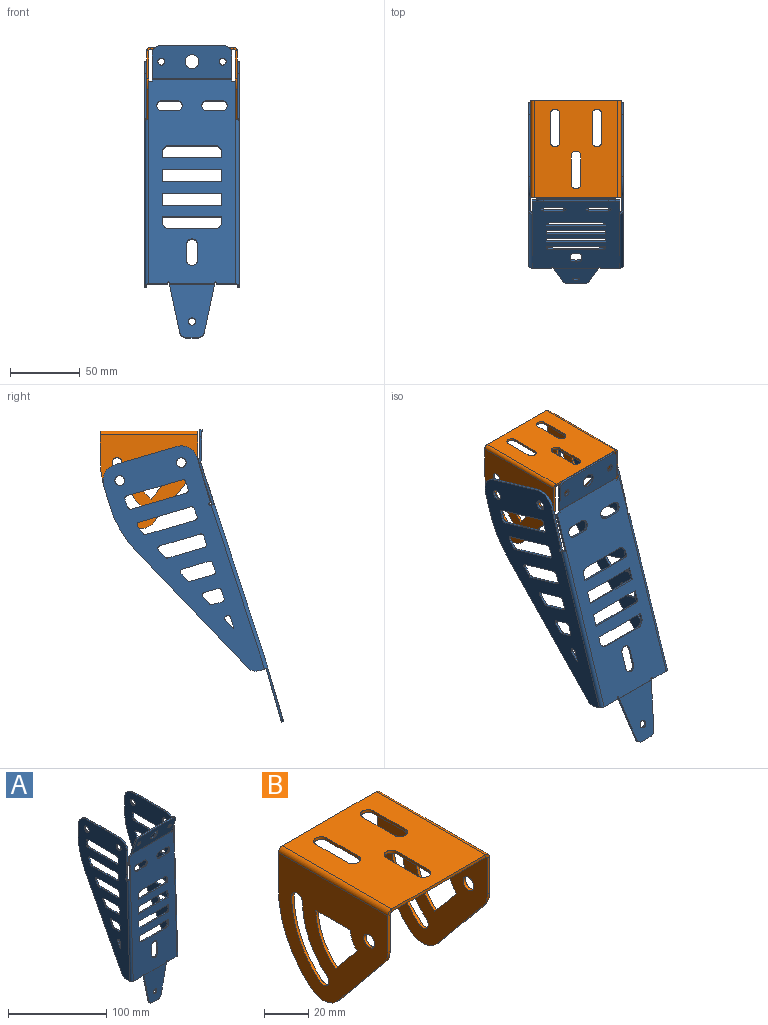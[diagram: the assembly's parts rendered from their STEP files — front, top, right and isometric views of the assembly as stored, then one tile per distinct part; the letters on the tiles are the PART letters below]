
ASSEMBLY  parts=2 mates=1
PART A: 208 faces, bbox 68x78.9x217.8 mm
  f0: plane 7.85x1.5mm, normal (0,0,-1), area 11.8mm2, adj f4,f5,f6,f7
  f1: plane 35.99x7.42mm, normal (0.98,0,-0.2), area 55.1mm2, adj f4,f5,f6,f196
  f2: cylinder r=2.75mm len=5.5mm, axis (0,-1,0), area 25.9mm2, adj f4,f5
  f3: plane 35.99x7.42mm, normal (-0.98,0,-0.2), area 55.1mm2, adj f4,f5,f7,f197
  f4: plane 39.98x32.49mm, normal (0,-1,0), area 939.2mm2, adj f0,f1,f2,f3,f6,f7,f198
  f5: plane 39.98x32.49mm, normal (0,1,0), area 939.2mm2, adj f0,f1,f2,f3,f6,f7,f199
  f6: cylinder r=5mm len=4.9mm, axis (0,-1,0), area 10.3mm2, adj f0,f1,f4,f5
  f7: cylinder r=5mm len=4.9mm, axis (0,1,0), area 10.3mm2, adj f0,f3,f4,f5
  f8: plane 33.42x1.5mm, normal (0,-1,0), area 50.1mm2, adj f9,f42,f43,f70
  f9: plane 171x74mm, normal (-1,0,0), area 6427.2mm2, adj f8,f10,f11,f12,f13,f14,f15,f16
  f10: plane 4.3x1.5mm, normal (0,0,-1), area 6.4mm2, adj f9,f43,f60,f205
  f11: plane 103.36x53.61mm, normal (0,0.89,-0.46), area 174.7mm2, adj f9,f43,f59,f60
  f12: plane 14.49x1.5mm, normal (0,1,0), area 21.7mm2, adj f9,f13,f43,f59
  f13: cylinder r=12mm len=12mm, axis (1,0,0), area 28.3mm2, adj f9,f12,f14,f43
  f14: plane 45.94x1.5mm, normal (0,0,1), area 68.9mm2, adj f9,f13,f42,f43
  f15: plane 41.22x1.5mm, normal (0,0,1), area 61.8mm2, adj f9,f43,f56,f57
  f16: plane 5.99x1.5mm, normal (0,1,-0.03), area 9mm2, adj f9,f43,f47,f56
  f17: plane 41.25x1.5mm, normal (0,0,-1), area 61.9mm2, adj f9,f43,f44,f47
  f18: plane 1.5x0.49mm, normal (0,-1,0), area 0.7mm2, adj f9,f41,f43,f44
  f19: plane 36.77x1.5mm, normal (0,0,1), area 55.2mm2, adj f9,f43,f45,f50
  f20: plane 5.99x1.5mm, normal (0,1,-0.03), area 9mm2, adj f9,f43,f48,f50
  f21: plane 38.8x1.5mm, normal (0,0,-1), area 58.2mm2, adj f9,f43,f48,f55
  f22: plane 5.99x1.5mm, normal (0,1,-0.03), area 9mm2, adj f9,f43,f51,f53
  f23: plane 30.15x1.5mm, normal (0,0,-1), area 45.2mm2, adj f9,f43,f46,f51
  f24: plane 5.97x3.1mm, normal (0,-0.89,0.46), area 10.1mm2, adj f9,f43,f46,f49
  f25: plane 5.99x1.5mm, normal (0,1,-0.03), area 9mm2, adj f9,f43,f62,f64
  f26: plane 20.16x1.5mm, normal (0,0,-1), area 30.2mm2, adj f9,f43,f58,f62
  f27: plane 5.97x3.1mm, normal (0,-0.89,0.46), area 10.1mm2, adj f9,f43,f52,f58
  f28: plane 5.99x1.5mm, normal (0,1,-0.03), area 9mm2, adj f9,f43,f66,f67
  f29: plane 10.17x1.5mm, normal (0,0,-1), area 15.3mm2, adj f9,f43,f54,f67
  f30: plane 5.98x3.1mm, normal (0,-0.89,0.46), area 10.1mm2, adj f9,f43,f54,f63
  f31: plane 8.05x1.5mm, normal (0,1,-0.03), area 12.1mm2, adj f9,f36,f43,f65
  f32: plane 1.5x0.19mm, normal (0,0,-1), area 0.3mm2, adj f9,f43,f61,f65
  f33: plane 7.07x3.67mm, normal (0,-0.89,0.46), area 11.9mm2, adj f9,f36,f43,f61
  f34: cylinder r=3.5mm len=7mm, axis (1,0,0), area 33mm2, adj f9,f43
  f35: cylinder r=3.5mm len=7mm, axis (1,0,0), area 33mm2, adj f9,f43
  f36: plane 1.5x0.55mm, normal (0,0,1), area 0.8mm2, adj f9,f31,f33,f43
  f37: plane 7.26x1.5mm, normal (0,0,1), area 10.9mm2, adj f9,f43,f63,f66
  f38: plane 17.26x1.5mm, normal (0,0,1), area 25.9mm2, adj f9,f43,f52,f64
  f39: plane 27.25x1.5mm, normal (0,0,1), area 40.9mm2, adj f9,f43,f49,f53
  f40: cylinder r=68.1mm len=6.14mm, axis (1,0,0), area 9.8mm2, adj f9,f43,f45,f55
  f41: cylinder r=68.1mm len=5.64mm, axis (1,0,0), area 8.5mm2, adj f9,f18,f43,f57
  f42: cylinder r=12mm len=12.06mm, axis (1,0,0), area 28.4mm2, adj f8,f9,f14,f43
  f43: plane 171x74mm, normal (1,0,0), area 6427.2mm2, adj f8,f10,f11,f12,f13,f14,f15,f16
  f44: cylinder r=2mm len=2mm, axis (-1,0,0), area 4.7mm2, adj f9,f17,f18,f43
  f45: cylinder r=2mm len=1.84mm, axis (1,0,0), area 3.5mm2, adj f9,f19,f40,f43
  f46: cylinder r=2mm len=2.92mm, axis (-1,0,0), area 6.1mm2, adj f9,f23,f24,f43
  f47: cylinder r=2mm len=2mm, axis (-1,0,0), area 4.6mm2, adj f9,f16,f17,f43
  f48: cylinder r=2mm len=2mm, axis (-1,0,0), area 4.6mm2, adj f9,f20,f21,f43
  f49: cylinder r=2mm len=1.78mm, axis (-1,0,0), area 3.3mm2, adj f9,f24,f39,f43
  f50: cylinder r=2mm len=2.06mm, axis (-1,0,0), area 4.8mm2, adj f9,f19,f20,f43
  f51: cylinder r=2mm len=2mm, axis (-1,0,0), area 4.6mm2, adj f9,f22,f23,f43
  f52: cylinder r=2mm len=1.78mm, axis (-1,0,0), area 3.3mm2, adj f9,f27,f38,f43
  f53: cylinder r=2mm len=2.06mm, axis (-1,0,0), area 4.8mm2, adj f9,f22,f39,f43
  f54: cylinder r=2mm len=2.92mm, axis (-1,0,0), area 6.1mm2, adj f9,f29,f30,f43
  f55: cylinder r=2mm len=2.61mm, axis (1,0,0), area 5.6mm2, adj f9,f21,f40,f43
  f56: cylinder r=2mm len=2.06mm, axis (-1,0,0), area 4.8mm2, adj f9,f15,f16,f43
  f57: cylinder r=2mm len=1.99mm, axis (1,0,0), area 4.5mm2, adj f9,f15,f41,f43
  f58: cylinder r=2mm len=2.92mm, axis (-1,0,0), area 6.1mm2, adj f9,f26,f27,f43
  f59: cylinder r=80mm len=36.84mm, axis (1,0,0), area 57.4mm2, adj f9,f11,f12,f43
  f60: cylinder r=8mm len=7.1mm, axis (-1,0,0), area 13.1mm2, adj f9,f10,f11,f43
  f61: cylinder r=2mm len=2.92mm, axis (-1,0,0), area 6.1mm2, adj f9,f32,f33,f43
  f62: cylinder r=2mm len=2mm, axis (-1,0,0), area 4.6mm2, adj f9,f25,f26,f43
  f63: cylinder r=2mm len=1.78mm, axis (-1,0,0), area 3.3mm2, adj f9,f30,f37,f43
  f64: cylinder r=2mm len=2.06mm, axis (-1,0,0), area 4.8mm2, adj f9,f25,f38,f43
  f65: cylinder r=2mm len=2mm, axis (-1,0,0), area 4.6mm2, adj f9,f31,f32,f43
  f66: cylinder r=2mm len=2.06mm, axis (-1,0,0), area 4.8mm2, adj f9,f28,f37,f43
  f67: cylinder r=2mm len=2mm, axis (-1,0,0), area 4.6mm2, adj f9,f28,f29,f43
  f68: cylinder r=0.8mm len=1.59mm, axis (-1,0,0), area 3.8mm2, adj f9,f43,f69,f70
  f69: plane 1.5x0.7mm, normal (0,0.03,1), area 1.1mm2, adj f9,f43,f68,f204
  f70: plane 1.5x0.75mm, normal (0,-0.03,-1), area 1.1mm2, adj f8,f9,f43,f68
  f71: plane 1.5x0.19mm, normal (0,0,-1), area 0.3mm2, adj f105,f106,f112,f113
  f72: plane 8.05x1.5mm, normal (0,1,-0.03), area 12.1mm2, adj f73,f105,f106,f112
  f73: plane 1.5x0.55mm, normal (0,0,1), area 0.8mm2, adj f72,f102,f105,f106
  f74: plane 10.17x1.5mm, normal (0,0,-1), area 15.3mm2, adj f105,f106,f109,f111
  f75: plane 5.99x1.5mm, normal (0,1,-0.03), area 9mm2, adj f105,f106,f107,f109
  f76: plane 7.26x1.5mm, normal (0,0,1), area 10.9mm2, adj f105,f106,f107,f116
  f77: plane 20.16x1.5mm, normal (0,0,-1), area 30.2mm2, adj f105,f106,f119,f124
  f78: plane 5.99x1.5mm, normal (0,1,-0.03), area 9mm2, adj f105,f106,f108,f119
  f79: plane 17.26x1.5mm, normal (0,0,1), area 25.9mm2, adj f105,f106,f108,f121
  f80: plane 30.15x1.5mm, normal (0,0,-1), area 45.2mm2, adj f105,f106,f122,f127
  f81: plane 5.99x1.5mm, normal (0,1,-0.03), area 9mm2, adj f105,f106,f120,f122
  f82: plane 27.25x1.5mm, normal (0,0,1), area 40.9mm2, adj f105,f106,f120,f126
  f83: plane 38.8x1.5mm, normal (0,0,-1), area 58.2mm2, adj f105,f106,f118,f125
  f84: plane 5.99x1.5mm, normal (0,1,-0.03), area 9mm2, adj f105,f106,f123,f125
  f85: plane 36.77x1.5mm, normal (0,0,1), area 55.2mm2, adj f105,f106,f123,f128
  f86: plane 1.5x0.49mm, normal (0,-1,0), area 0.7mm2, adj f97,f105,f106,f130
  f87: plane 41.25x1.5mm, normal (0,0,-1), area 61.9mm2, adj f105,f106,f114,f130
  f88: plane 5.99x1.5mm, normal (0,1,-0.03), area 9mm2, adj f105,f106,f114,f115
  f89: plane 41.22x1.5mm, normal (0,0,1), area 61.8mm2, adj f105,f106,f115,f129
  f90: plane 45.94x1.5mm, normal (0,0,1), area 68.9mm2, adj f91,f96,f105,f106
  f91: cylinder r=12mm len=12mm, axis (1,0,0), area 28.3mm2, adj f90,f92,f105,f106
  f92: plane 14.49x1.5mm, normal (0,1,0), area 21.7mm2, adj f91,f105,f106,f117
  f93: plane 103.36x53.61mm, normal (0,0.89,-0.46), area 174.7mm2, adj f105,f106,f110,f117
  f94: plane 4.3x1.5mm, normal (0,0,-1), area 6.4mm2, adj f105,f106,f110,f201
  f95: plane 33.42x1.5mm, normal (0,-1,0), area 50.1mm2, adj f96,f105,f106,f131
  f96: cylinder r=12mm len=12.06mm, axis (1,0,0), area 28.4mm2, adj f90,f95,f105,f106
  f97: cylinder r=68.1mm len=5.64mm, axis (1,0,0), area 8.5mm2, adj f86,f105,f106,f129
  f98: cylinder r=68.1mm len=6.14mm, axis (1,0,0), area 9.8mm2, adj f105,f106,f118,f128
  f99: plane 5.97x3.1mm, normal (0,-0.89,0.46), area 10.1mm2, adj f105,f106,f126,f127
  f100: plane 5.97x3.1mm, normal (0,-0.89,0.46), area 10.1mm2, adj f105,f106,f121,f124
  f101: plane 5.98x3.1mm, normal (0,-0.89,0.46), area 10.1mm2, adj f105,f106,f111,f116
  f102: plane 7.07x3.67mm, normal (0,-0.89,0.46), area 11.9mm2, adj f73,f105,f106,f113
  f103: cylinder r=3.5mm len=7mm, axis (1,0,0), area 33mm2, adj f105,f106
  f104: cylinder r=3.5mm len=7mm, axis (1,0,0), area 33mm2, adj f105,f106
  f105: plane 171x74mm, normal (-1,0,0), area 6427.2mm2, adj f71,f72,f73,f74,f75,f76,f77,f78
  f106: plane 171x74mm, normal (1,0,0), area 6427.2mm2, adj f71,f72,f73,f74,f75,f76,f77,f78
  f107: cylinder r=2mm len=2.06mm, axis (1,0,0), area 4.8mm2, adj f75,f76,f105,f106
  f108: cylinder r=2mm len=2.06mm, axis (1,0,0), area 4.8mm2, adj f78,f79,f105,f106
  f109: cylinder r=2mm len=2mm, axis (1,0,0), area 4.6mm2, adj f74,f75,f105,f106
  f110: cylinder r=8mm len=7.1mm, axis (1,0,0), area 13.1mm2, adj f93,f94,f105,f106
  f111: cylinder r=2mm len=2.92mm, axis (1,0,0), area 6.1mm2, adj f74,f101,f105,f106
  f112: cylinder r=2mm len=2mm, axis (1,0,0), area 4.6mm2, adj f71,f72,f105,f106
  f113: cylinder r=2mm len=2.92mm, axis (1,0,0), area 6.1mm2, adj f71,f102,f105,f106
  f114: cylinder r=2mm len=2mm, axis (1,0,0), area 4.6mm2, adj f87,f88,f105,f106
  f115: cylinder r=2mm len=2.06mm, axis (1,0,0), area 4.8mm2, adj f88,f89,f105,f106
  f116: cylinder r=2mm len=1.78mm, axis (1,0,0), area 3.3mm2, adj f76,f101,f105,f106
  f117: cylinder r=80mm len=36.84mm, axis (-1,0,0), area 57.4mm2, adj f92,f93,f105,f106
  f118: cylinder r=2mm len=2.61mm, axis (1,0,0), area 5.6mm2, adj f83,f98,f105,f106
  f119: cylinder r=2mm len=2mm, axis (1,0,0), area 4.6mm2, adj f77,f78,f105,f106
  f120: cylinder r=2mm len=2.06mm, axis (1,0,0), area 4.8mm2, adj f81,f82,f105,f106
  f121: cylinder r=2mm len=1.78mm, axis (1,0,0), area 3.3mm2, adj f79,f100,f105,f106
  f122: cylinder r=2mm len=2mm, axis (1,0,0), area 4.6mm2, adj f80,f81,f105,f106
  f123: cylinder r=2mm len=2.06mm, axis (1,0,0), area 4.8mm2, adj f84,f85,f105,f106
  f124: cylinder r=2mm len=2.92mm, axis (1,0,0), area 6.1mm2, adj f77,f100,f105,f106
  f125: cylinder r=2mm len=2mm, axis (1,0,0), area 4.6mm2, adj f83,f84,f105,f106
  f126: cylinder r=2mm len=1.78mm, axis (1,0,0), area 3.3mm2, adj f82,f99,f105,f106
  f127: cylinder r=2mm len=2.92mm, axis (1,0,0), area 6.1mm2, adj f80,f99,f105,f106
  f128: cylinder r=2mm len=1.84mm, axis (1,0,0), area 3.5mm2, adj f85,f98,f105,f106
  f129: cylinder r=2mm len=1.99mm, axis (1,0,0), area 4.5mm2, adj f89,f97,f105,f106
  f130: cylinder r=2mm len=2mm, axis (1,0,0), area 4.7mm2, adj f86,f87,f105,f106
  f131: plane 1.5x0.75mm, normal (0,-0.03,-1), area 1.1mm2, adj f95,f105,f106,f132
  f132: cylinder r=0.8mm len=1.59mm, axis (1,0,0), area 3.8mm2, adj f105,f106,f131,f133
  f133: plane 1.5x0.7mm, normal (0,0.03,1), area 1.1mm2, adj f105,f106,f132,f200
  f134: plane 29.09x2.44mm, normal (-1,0,0), area 43.6mm2, adj f136,f137,f138,f200
  f135: plane 13.66x1.5mm, normal (0,-0.03,-1), area 20.5mm2, adj f136,f137,f179,f201
  f136: plane 154.56x63mm, normal (0,-1,0.03), area 7809.2mm2, adj f134,f135,f138,f139,f140,f141,f142,f143
  f137: plane 154.56x63mm, normal (0,1,-0.03), area 7809.2mm2, adj f134,f135,f138,f139,f140,f141,f142,f143
  f138: plane 3x1.5mm, normal (0,0.03,1), area 4.5mm2, adj f134,f136,f137,f180
  f139: plane 13.66x1.5mm, normal (0,-0.03,-1), area 20.5mm2, adj f136,f137,f174,f205
  f140: plane 29.09x2.44mm, normal (1,0,0), area 43.6mm2, adj f136,f137,f169,f204
  f141: plane 10.25x1.5mm, normal (0,-0.03,-1), area 15.4mm2, adj f136,f137,f142,f168
  f142: cylinder r=4mm len=8.04mm, axis (0,1,-0.03), area 18.8mm2, adj f136,f137,f141,f143
  f143: plane 10.25x1.5mm, normal (0,0.03,1), area 15.4mm2, adj f136,f137,f142,f168
  f144: plane 10.25x1.5mm, normal (0,-0.03,-1), area 15.4mm2, adj f136,f137,f145,f167
  f145: cylinder r=4mm len=8.04mm, axis (0,1,-0.03), area 18.8mm2, adj f136,f137,f144,f146
  f146: plane 10.25x1.5mm, normal (0,0.03,1), area 15.4mm2, adj f136,f137,f145,f167
  f147: plane 4.05x1.63mm, normal (1,0,0), area 6mm2, adj f136,f137,f166,f171
  f148: plane 32.5x1.5mm, normal (0,-0.03,-1), area 48.7mm2, adj f136,f137,f170,f171
  f149: plane 4.05x1.63mm, normal (-1,0,0), area 6mm2, adj f136,f137,f166,f170
  f150: plane 9.04x1.79mm, normal (1,0,0), area 13.5mm2, adj f136,f137,f151,f165
  f151: plane 42.5x1.5mm, normal (0,-0.03,-1), area 63.7mm2, adj f136,f137,f150,f152
  f152: plane 9.04x1.79mm, normal (-1,0,0), area 13.5mm2, adj f136,f137,f151,f165
  f153: plane 9.04x1.79mm, normal (-1,0,0), area 13.5mm2, adj f136,f137,f154,f164
  f154: plane 42.5x1.5mm, normal (0,0.03,1), area 63.8mm2, adj f136,f137,f153,f155
  f155: plane 9.04x1.79mm, normal (1,0,0), area 13.5mm2, adj f136,f137,f154,f164
  f156: plane 4.05x1.63mm, normal (1,0,0), area 6mm2, adj f136,f137,f157,f173
  f157: plane 42.5x1.5mm, normal (0,-0.03,-1), area 63.8mm2, adj f136,f137,f156,f158
  f158: plane 4.05x1.63mm, normal (-1,0,0), area 6mm2, adj f136,f137,f157,f172
  f159: plane 12.04x1.89mm, normal (1,0,0), area 18mm2, adj f136,f137,f160,f162
  f160: cylinder r=4mm len=8mm, axis (0,1,-0.03), area 18.8mm2, adj f136,f137,f159,f161
  f161: plane 12.04x1.89mm, normal (-1,0,0), area 18mm2, adj f136,f137,f160,f162
  f162: cylinder r=4mm len=8mm, axis (0,1,-0.03), area 18.8mm2, adj f136,f137,f159,f161
  f163: plane 32.5x1.5mm, normal (0,0.03,1), area 48.7mm2, adj f136,f137,f172,f173
  f164: plane 42.5x1.5mm, normal (0,-0.03,-1), area 63.7mm2, adj f136,f137,f153,f155
  f165: plane 42.5x1.5mm, normal (0,0.03,1), area 63.7mm2, adj f136,f137,f150,f152
  f166: plane 42.5x1.5mm, normal (0,0.03,1), area 63.7mm2, adj f136,f137,f147,f149
  f167: cylinder r=4mm len=8.04mm, axis (0,1,-0.03), area 18.8mm2, adj f136,f137,f144,f146
  f168: cylinder r=4mm len=8.04mm, axis (0,1,-0.03), area 18.8mm2, adj f136,f137,f141,f143
  f169: plane 3x1.5mm, normal (0,0.03,1), area 4.5mm2, adj f136,f137,f140,f181
  f170: cylinder r=5mm len=5.05mm, axis (0,1,-0.03), area 11.8mm2, adj f136,f137,f148,f149
  f171: cylinder r=5mm len=5.05mm, axis (0,1,-0.03), area 11.8mm2, adj f136,f137,f147,f148
  f172: cylinder r=5mm len=5.05mm, axis (0,1,-0.03), area 11.8mm2, adj f136,f137,f158,f163
  f173: cylinder r=5mm len=5.05mm, axis (0,1,-0.03), area 11.8mm2, adj f136,f137,f156,f163
  f174: plane 1.52x0.77mm, normal (-1,0,0), area 1.1mm2, adj f136,f137,f139,f175
  f175: cylinder r=0.8mm len=1.59mm, axis (0,1,-0.03), area 3.8mm2, adj f136,f137,f174,f176
  f176: plane 1.52x0.75mm, normal (1,0,0), area 1.1mm2, adj f136,f137,f175,f196
  f177: plane 1.52x0.75mm, normal (-1,0,0), area 1.1mm2, adj f136,f137,f178,f197
  f178: cylinder r=0.8mm len=1.59mm, axis (0,1,-0.03), area 3.8mm2, adj f136,f137,f177,f179
  f179: plane 1.52x0.77mm, normal (1,0,0), area 1.1mm2, adj f135,f136,f137,f178
  f180: plane 1.55x1.55mm, normal (-1,0,0), area 2.3mm2, adj f136,f137,f138,f192
  f181: plane 1.55x1.55mm, normal (1,0,0), area 2.3mm2, adj f136,f137,f169,f193
  f182: plane 47x1.43mm, normal (0,-0.31,0.95), area 70.5mm2, adj f188,f189,f190,f191
  f183: plane 18.1x7.21mm, normal (-1,0,0), area 27.8mm2, adj f188,f189,f190,f192
  f184: cylinder r=2.5mm len=5.22mm, axis (0,-0.95,-0.31), area 23.6mm2, adj f188,f189
  f185: cylinder r=2.5mm len=5.22mm, axis (0,-0.95,-0.31), area 23.6mm2, adj f188,f189
  f186: cylinder r=5mm len=10mm, axis (0,-0.95,-0.31), area 47.1mm2, adj f188,f189
  f187: plane 18.1x7.21mm, normal (1,0,0), area 27.8mm2, adj f188,f189,f191,f193
  f188: plane 57x22.39mm, normal (0,-0.95,-0.31), area 1214.3mm2, adj f182,f183,f184,f185,f186,f187,f190,f191
  f189: plane 57x22.39mm, normal (0,0.95,0.31), area 1214.3mm2, adj f182,f183,f184,f185,f186,f187,f190,f191
  f190: cylinder r=5mm len=5.22mm, axis (0,-0.95,-0.31), area 11.8mm2, adj f182,f183,f188,f189
  f191: cylinder r=5mm len=5.22mm, axis (0,-0.95,-0.31), area 11.8mm2, adj f182,f187,f188,f189
  f192: plane 1.55x0.86mm, normal (-1,0,0), area 0.9mm2, adj f180,f183,f194,f195
  f193: plane 1.55x0.86mm, normal (1,0,0), area 0.9mm2, adj f181,f187,f194,f195
  f194: cylinder r=2.5mm len=57mm, axis (-1,0,0), area 49.7mm2, adj f137,f189,f192,f193
  f195: cylinder r=1mm len=57mm, axis (-1,0,0), area 19.9mm2, adj f136,f188,f192,f193
  f196: plane 1.5x0.08mm, normal (1,0,0), area 0.1mm2, adj f1,f176,f198,f199
  f197: plane 1.5x0.08mm, normal (-1,0,0), area 0.1mm2, adj f3,f177,f198,f199
  f198: cylinder r=2.5mm len=32.49mm, axis (1,0,0), area 2.6mm2, adj f4,f136,f196,f197
  f199: cylinder r=1mm len=32.49mm, axis (1,0,0), area 1mm2, adj f5,f137,f196,f197
  f200: plane 2.5x2.5mm, normal (0,0.03,1), area 4.1mm2, adj f133,f134,f202,f203
  f201: bspline ~2.5x2.5mm, area 4.1mm2, adj f94,f135,f202,f203
  f202: cylinder r=2.5mm len=124.1mm, axis (0,0.03,1), area 487.2mm2, adj f105,f136,f200,f201
  f203: cylinder r=1mm len=124.05mm, axis (0,0.03,1), area 194.9mm2, adj f106,f137,f200,f201
  f204: plane 2.5x2.5mm, normal (0,0.03,1), area 4.1mm2, adj f69,f140,f206,f207
  f205: bspline ~2.5x2.5mm, area 4.1mm2, adj f10,f139,f206,f207
  f206: cylinder r=2.5mm len=124.1mm, axis (0,0.03,1), area 487.2mm2, adj f43,f136,f204,f205
  f207: cylinder r=1mm len=124.05mm, axis (0,0.03,1), area 194.9mm2, adj f9,f137,f204,f205
PART B: 58 faces, bbox 65x70x70 mm
  f0: plane 20x1.5mm, normal (-1,0,0), area 30mm2, adj f1,f13,f14,f15
  f1: cylinder r=3.5mm len=7mm, axis (0,0,1), area 16.5mm2, adj f0,f2,f14,f15
  f2: plane 20x1.5mm, normal (1,0,0), area 30mm2, adj f1,f13,f14,f15
  f3: plane 20x1.5mm, normal (-1,0,0), area 30mm2, adj f4,f12,f14,f15
  f4: cylinder r=3.5mm len=7mm, axis (0,0,1), area 16.5mm2, adj f3,f5,f14,f15
  f5: plane 20x1.5mm, normal (1,0,0), area 30mm2, adj f4,f12,f14,f15
  f6: plane 20x1.5mm, normal (1,0,0), area 30mm2, adj f7,f11,f14,f15
  f7: cylinder r=3.5mm len=7mm, axis (0,0,1), area 16.5mm2, adj f6,f8,f14,f15
  f8: plane 20x1.5mm, normal (-1,0,0), area 30mm2, adj f7,f11,f14,f15
  f9: plane 60x1.5mm, normal (0,1,0), area 90mm2, adj f14,f15,f34,f54
  f10: plane 60x1.5mm, normal (0,-1,0), area 90mm2, adj f14,f15,f33,f55
  f11: cylinder r=3.5mm len=7mm, axis (0,0,1), area 16.5mm2, adj f6,f8,f14,f15
  f12: cylinder r=3.5mm len=7mm, axis (0,0,1), area 16.5mm2, adj f3,f5,f14,f15
  f13: cylinder r=3.5mm len=7mm, axis (0,0,1), area 16.5mm2, adj f0,f2,f14,f15
  f14: plane 70x60mm, normal (0,0,1), area 3664.5mm2, adj f0,f1,f2,f3,f4,f5,f6,f7
  f15: plane 70x60mm, normal (0,0,-1), area 3664.5mm2, adj f0,f1,f2,f3,f4,f5,f6,f7
  f16: plane 20x1.5mm, normal (0,1,0), area 30mm2, adj f30,f31,f32,f34
  f17: plane 20x1.5mm, normal (0,-1,0), area 30mm2, adj f18,f31,f32,f33
  f18: cylinder r=12mm len=7.63mm, axis (1,0,0), area 12.4mm2, adj f17,f19,f31,f32
  f19: plane 35.5x29.25mm, normal (0,-0.77,-0.64), area 69mm2, adj f18,f20,f31,f32
  f20: cylinder r=12mm len=16.89mm, axis (1,0,0), area 28.3mm2, adj f19,f30,f31,f32
  f21: plane 16.98x13.99mm, normal (0,0.77,0.64), area 33mm2, adj f22,f29,f31,f32
  f22: cylinder r=12mm len=9.26mm, axis (1,0,0), area 15.9mm2, adj f21,f23,f31,f32
  f23: plane 22x1.5mm, normal (0,0,-1), area 33mm2, adj f22,f29,f31,f32
  f24: cylinder r=49.5mm len=38.2mm, axis (1,0,0), area 65.5mm2, adj f25,f27,f31,f32
  f25: cylinder r=3.5mm len=6.2mm, axis (1,0,0), area 16.5mm2, adj f24,f26,f31,f32
  f26: cylinder r=42.5mm len=32.8mm, axis (1,0,0), area 56.2mm2, adj f25,f27,f31,f32
  f27: cylinder r=3.5mm len=7mm, axis (1,0,0), area 16.5mm2, adj f24,f26,f31,f32
  f28: cylinder r=3.5mm len=7mm, axis (1,0,0), area 33mm2, adj f31,f32
  f29: cylinder r=34mm len=26.24mm, axis (1,0,0), area 45mm2, adj f21,f23,f31,f32
  f30: cylinder r=58mm len=44.76mm, axis (1,0,0), area 76.7mm2, adj f16,f20,f31,f32
  f31: plane 70x67.5mm, normal (1,0,0), area 2790.6mm2, adj f16,f17,f18,f19,f20,f21,f22,f23
  f32: plane 70x67.5mm, normal (-1,0,0), area 2790.6mm2, adj f16,f17,f18,f19,f20,f21,f22,f23
  f33: plane 2.5x2.5mm, normal (0,-1,0), area 4.1mm2, adj f10,f17,f35,f36
  f34: plane 2.5x2.5mm, normal (0,1,0), area 4.1mm2, adj f9,f16,f35,f36
  f35: cylinder r=2.5mm len=70mm, axis (0,-1,0), area 274.9mm2, adj f14,f31,f33,f34
  f36: cylinder r=1mm len=70mm, axis (0,-1,0), area 110mm2, adj f15,f32,f33,f34
  f37: cylinder r=12mm len=16.89mm, axis (-1,0,0), area 28.3mm2, adj f38,f51,f52,f53
  f38: plane 35.5x29.25mm, normal (0,-0.77,-0.64), area 69mm2, adj f37,f39,f52,f53
  f39: cylinder r=12mm len=7.63mm, axis (-1,0,0), area 12.4mm2, adj f38,f40,f52,f53
  f40: plane 20x1.5mm, normal (0,-1,0), area 30mm2, adj f39,f52,f53,f55
  f41: plane 20x1.5mm, normal (0,1,0), area 30mm2, adj f51,f52,f53,f54
  f42: cylinder r=42.5mm len=32.8mm, axis (-1,0,0), area 56.2mm2, adj f43,f50,f52,f53
  f43: cylinder r=3.5mm len=6.2mm, axis (-1,0,0), area 16.5mm2, adj f42,f44,f52,f53
  f44: cylinder r=49.5mm len=38.2mm, axis (-1,0,0), area 65.5mm2, adj f43,f50,f52,f53
  f45: plane 22x1.5mm, normal (0,0,-1), area 33mm2, adj f46,f49,f52,f53
  f46: cylinder r=12mm len=9.26mm, axis (-1,0,0), area 15.9mm2, adj f45,f47,f52,f53
  f47: plane 16.98x13.99mm, normal (0,0.77,0.64), area 33mm2, adj f46,f49,f52,f53
  f48: cylinder r=3.5mm len=7mm, axis (-1,0,0), area 33mm2, adj f52,f53
  f49: cylinder r=34mm len=26.24mm, axis (-1,0,0), area 45mm2, adj f45,f47,f52,f53
  f50: cylinder r=3.5mm len=7mm, axis (-1,0,0), area 16.5mm2, adj f42,f44,f52,f53
  f51: cylinder r=58mm len=44.76mm, axis (-1,0,0), area 76.7mm2, adj f37,f41,f52,f53
  f52: plane 70x67.5mm, normal (-1,0,0), area 2790.6mm2, adj f37,f38,f39,f40,f41,f42,f43,f44
  f53: plane 70x67.5mm, normal (1,0,0), area 2790.6mm2, adj f37,f38,f39,f40,f41,f42,f43,f44
  f54: plane 2.5x2.5mm, normal (0,1,0), area 4.1mm2, adj f9,f41,f56,f57
  f55: plane 2.5x2.5mm, normal (0,-1,0), area 4.1mm2, adj f10,f40,f56,f57
  f56: cylinder r=2.5mm len=70mm, axis (0,1,0), area 274.9mm2, adj f14,f52,f54,f55
  f57: cylinder r=1mm len=70mm, axis (0,1,0), area 110mm2, adj f15,f53,f54,f55
PLACE A rot(axis=(-1,0,0),16.3deg) t=(-36.2,0.15,-33.37)mm
PLACE B t=(-36.2,24.37,-41.68)mm fixed
MATE revolute B.f39 <-> A.f96  axis (-1,0,0) through (-68.7,41.37,47.32)mm
